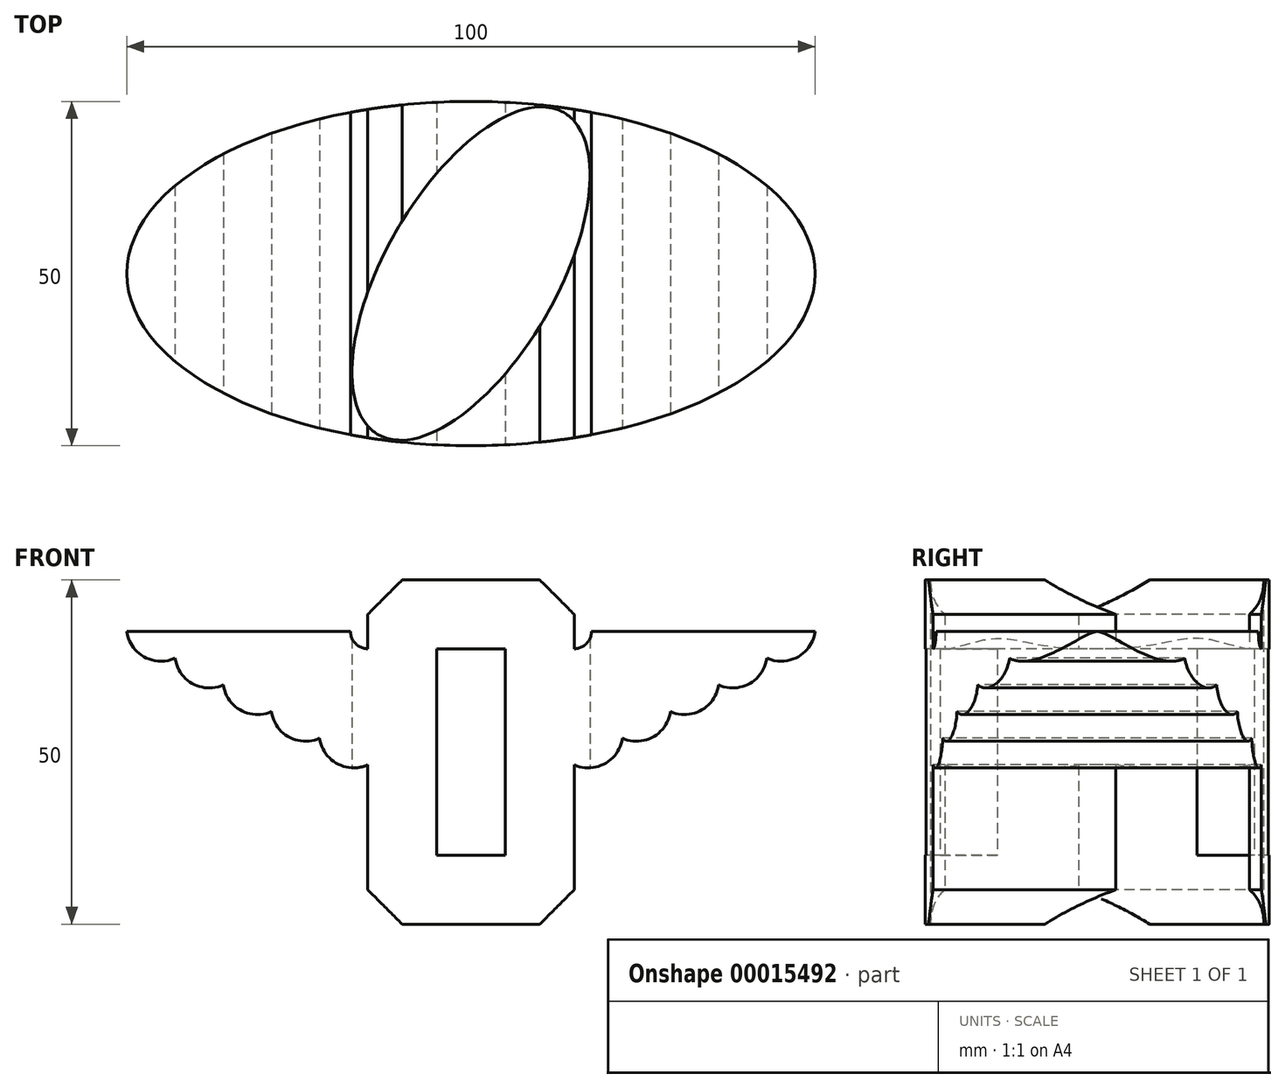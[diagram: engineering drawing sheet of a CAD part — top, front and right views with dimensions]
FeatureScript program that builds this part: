
annotation { "Feature Type Name" : "Feature", "Feature Type Description" : "" }
export const myFeature = defineFeature(function(context is Context, id is Id, definition is map)
    precondition{}
    {
        {
            var Q0;
            Q0=qCreatedBy(makeId("Top.planeOp"),FACE);
            var sketch = newSketch(context, id + "F0", { "sketchPlane" : qUnion([Q0])});
            skEllipse(sketch, "E0", {"center": v(0, 0) * mm, "majorRadius": 50 * mm, "minorRadius": 25 * mm, "majorAxis": v(1, 0)});
            skEllipse(sketch, "E1", {"center": v(0, 0) * mm, "majorRadius": 27 * mm, "minorRadius": 12.5 * mm, "majorAxis": v(0.5, 0.87)});
            skLineSegment(sketch, "E2", {"start": v(0, 0) * mm, "end": v(13.5, 23.38) * mm, "construction": true});
            skLineSegment(sketch, "E3", {"start": v(0, 0) * mm, "end": v(50, 0) * mm, "construction": true});
            skSolve(sketch);
        }
        {
            var Q0;
            Q0 = qSketchRegion(id + "F0", true);
            extrude(context, id + "F1", {"entities" : qUnion([Q0]), "depth" : 50 * mm});
        }
        {
            var Q0;
            Q0=qCreatedBy(makeId("Front.planeOp"),FACE);
            var sketch = newSketch(context, id + "F2", { "sketchPlane" : qUnion([Q0])});
            skLineSegment(sketch, "E4", {"start": v(-50, 42.5) * mm, "end": v(-17.5, 42.5) * mm});
            skLineSegment(sketch, "E5", {"start": v(-15, 40) * mm, "end": v(-15, 45) * mm});
            skLineSegment(sketch, "E6", {"start": v(-15, 45) * mm, "end": v(-10, 50) * mm});
            skLineSegment(sketch, "E7", {"start": v(-10, 50) * mm, "end": v(0, 50) * mm});
            skLineSegment(sketch, "E8", {"start": v(0, 50) * mm, "end": v(0, 0) * mm, "construction": true});
            skLineSegment(sketch, "E9", {"start": v(0, 0) * mm, "end": v(-10, 0) * mm});
            skLineSegment(sketch, "E10", {"start": v(-10, 0) * mm, "end": v(-15, 5) * mm});
            skLineSegment(sketch, "E11", {"start": v(-15, 5) * mm, "end": v(-15, 23.14) * mm});
            skLineSegment(sketch, "E12", {"start": v(-15, 23.14) * mm, "end": v(-50, 42.5) * mm, "construction": true});
            skArc(sketch, "E13", {"start": v(-17.5, 42.5) * mm, "mid": v(-16.77, 40.73) * mm, "end": v(-15, 40) * mm});
            skLineSegment(sketch, "E14.MirrorCS", {"start": v(15, 40) * mm, "end": v(15, 45) * mm});
            skLineSegment(sketch, "E15.MirrorCS", {"start": v(15, 45) * mm, "end": v(10, 50) * mm});
            skArc(sketch, "E16.MirrorCS", {"start": v(17.5, 42.5) * mm, "mid": v(16.77, 40.73) * mm, "end": v(15, 40) * mm});
            skLineSegment(sketch, "E17.MirrorCS", {"start": v(15, 23.14) * mm, "end": v(50, 42.5) * mm, "construction": true});
            skLineSegment(sketch, "E18.MirrorCS", {"start": v(15, 5) * mm, "end": v(15, 23.14) * mm});
            skLineSegment(sketch, "E19.MirrorCS", {"start": v(10, 0) * mm, "end": v(15, 5) * mm});
            skLineSegment(sketch, "E20.MirrorCS", {"start": v(50, 42.5) * mm, "end": v(17.5, 42.5) * mm});
            skLineSegment(sketch, "E21.bottom", {"start": v(-69, 62.78) * mm, "end": v(91.18, 62.78) * mm});
            skLineSegment(sketch, "E21.top", {"start": v(-69, -17.94) * mm, "end": v(91.18, -17.94) * mm});
            skLineSegment(sketch, "E21.left", {"start": v(-69, 62.78) * mm, "end": v(-69, -17.94) * mm});
            skLineSegment(sketch, "E21.right", {"start": v(91.18, 62.78) * mm, "end": v(91.18, -17.94) * mm});
            skLineSegment(sketch, "E22", {"start": v(0, 50) * mm, "end": v(10, 50) * mm});
            skLineSegment(sketch, "E23", {"start": v(10, 0) * mm, "end": v(0, 0) * mm});
            skArc(sketch, "E24", {"start": v(-22, 27) * mm, "mid": v(-19.47, 23.32) * mm, "end": v(-15, 23.14) * mm});
            skArc(sketch, "E25", {"start": v(-29, 30.88) * mm, "mid": v(-26.47, 27.2) * mm, "end": v(-22, 27) * mm});
            skArc(sketch, "E26", {"start": v(-36, 34.75) * mm, "mid": v(-33.47, 31.07) * mm, "end": v(-29, 30.88) * mm});
            skArc(sketch, "E27", {"start": v(-43, 38.63) * mm, "mid": v(-40.47, 34.94) * mm, "end": v(-36, 34.75) * mm});
            skArc(sketch, "E28", {"start": v(-50, 42.5) * mm, "mid": v(-47.47, 38.81) * mm, "end": v(-43, 38.63) * mm});
            skArc(sketch, "E29.MirrorCS", {"start": v(22, 27) * mm, "mid": v(19.47, 23.32) * mm, "end": v(15, 23.14) * mm});
            skArc(sketch, "E30.MirrorCS", {"start": v(29, 30.88) * mm, "mid": v(26.47, 27.2) * mm, "end": v(22, 27) * mm});
            skArc(sketch, "E31.MirrorCS", {"start": v(36, 34.75) * mm, "mid": v(33.47, 31.07) * mm, "end": v(29, 30.88) * mm});
            skArc(sketch, "E32.MirrorCS", {"start": v(43, 38.63) * mm, "mid": v(40.47, 34.94) * mm, "end": v(36, 34.75) * mm});
            skArc(sketch, "E33.MirrorCS", {"start": v(50, 42.5) * mm, "mid": v(47.47, 38.81) * mm, "end": v(43, 38.63) * mm});
            skSolve(sketch);
        }
        {
            var Q0;
            Q0 = qSketchRegion(id + "F2", true);
            extrude(context, id + "F3", {"entities" : qUnion([Q0]), "operationType" : NewBodyOperationType.REMOVE, "endBound" : BoundingType.SYMMETRIC, "oppositeDirection" : true, "depth" : 274.53 * mm});
        }
        {
            var Q0;
            Q0=qCreatedBy(makeId("Front.planeOp"),FACE);
            var sketch = newSketch(context, id + "F4", { "sketchPlane" : qUnion([Q0])});
            skLineSegment(sketch, "E34.bottom", {"start": v(-5, 40) * mm, "end": v(5, 40) * mm});
            skLineSegment(sketch, "E34.top", {"start": v(-5, 10) * mm, "end": v(5, 10) * mm});
            skLineSegment(sketch, "E34.left", {"start": v(-5, 40) * mm, "end": v(-5, 10) * mm});
            skLineSegment(sketch, "E34.right", {"start": v(5, 40) * mm, "end": v(5, 10) * mm});
            skSolve(sketch);
        }
        {
            var Q0;
            Q0 = qSketchRegion(id + "F4", true);
            extrude(context, id + "F5", {"entities" : qUnion([Q0]), "operationType" : NewBodyOperationType.REMOVE, "endBound" : BoundingType.SYMMETRIC, "oppositeDirection" : true, "depth" : 141.23 * mm});
        }
    });
